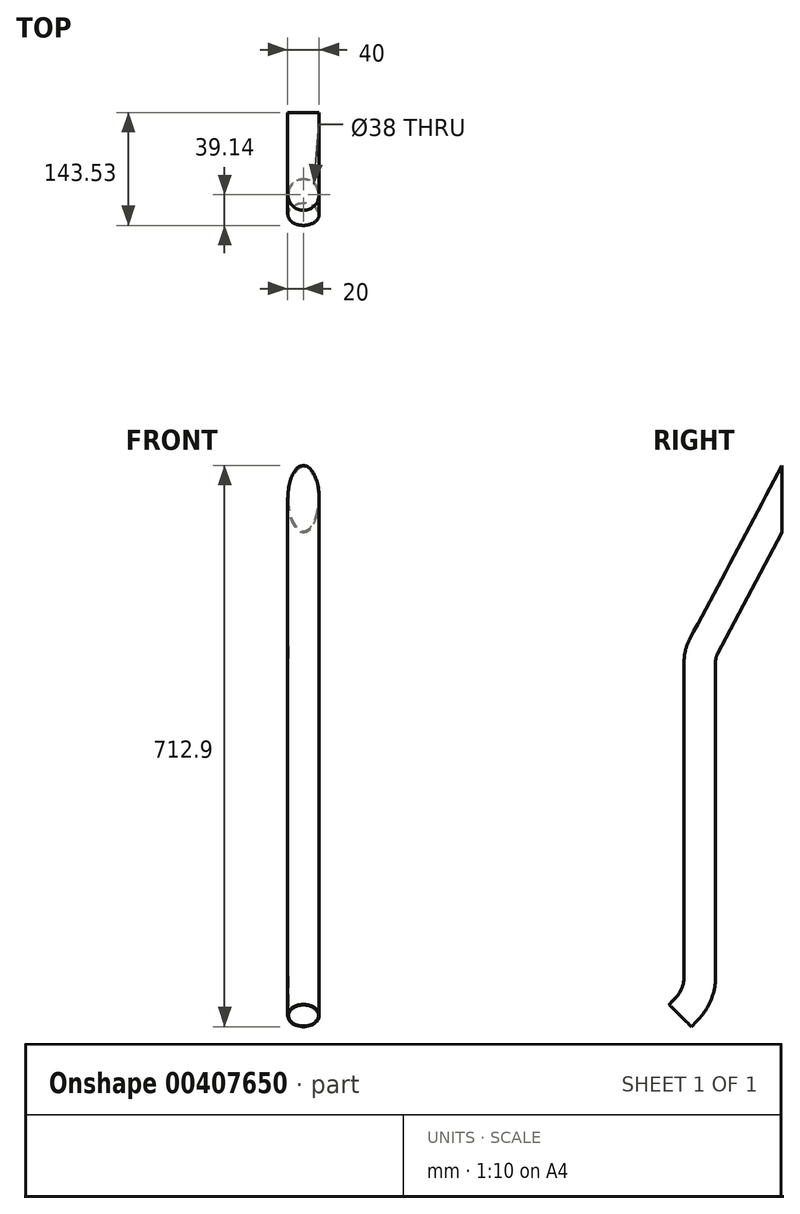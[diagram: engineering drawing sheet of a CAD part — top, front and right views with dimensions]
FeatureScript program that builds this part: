
annotation { "Feature Type Name" : "Feature", "Feature Type Description" : "" }
export const myFeature = defineFeature(function(context is Context, id is Id, definition is map)
    precondition{}
    {
        {
            var Q0;
            Q0=qCreatedBy(makeId("Right.planeOp"),FACE);
            var sketch = newSketch(context, id + "F0", { "sketchPlane" : qUnion([Q0])});
            skLineSegment(sketch, "E0", {"start": v(0, 0) * mm, "end": v(7.43, 7.43) * mm});
            skLineSegment(sketch, "E1", {"start": v(25, 49.85) * mm, "end": v(25, 449.85) * mm});
            skLineSegment(sketch, "E2", {"start": v(29.68, 468.63) * mm, "end": v(147.05, 689.37) * mm});
            skPoint(sketch, "E3.visualSharp", {"position": v(25, 25) * mm});
            skArc(sketch, "E3.filletArc", {"start": v(7.43, 7.43) * mm, "mid": v(20.43, 26.9) * mm, "end": v(25, 49.85) * mm});
            skPoint(sketch, "E4.visualSharp", {"position": v(25, 459.83) * mm});
            skArc(sketch, "E4.filletArc", {"start": v(29.68, 468.63) * mm, "mid": v(26.19, 459.53) * mm, "end": v(25, 449.85) * mm});
            skPoint(sketch, "E5.visualSharp", {"position": v(83.86, 570.52) * mm});
            skLineSegment(sketch, "E6", {"start": v(0, 0) * mm, "end": v(15.6, -15.6) * mm});
            skSolve(sketch);
        }
        {
            var Q0;
            Q0=sQuery(id+"F0.wireOp",EDGE,"E6");
            cPlane(context, id + "F1", {"entities" : qUnion([Q0]), "cplaneType" : CPlaneType.LINE_ANGLE, "offset" : 25 * mm, "angle" : 0 * degree, "width" : 150 * mm, "height" : 150 * mm});
        }
        {
            var Q0;
            Q0=qCreatedBy(id+"F1.planeOp",FACE);
            var sketch = newSketch(context, id + "F2", { "sketchPlane" : qUnion([Q0])});
            skCircle(sketch, "E7", {"center": v(0, 0) * mm, "radius": 20 * mm});
            skCircle(sketch, "E8.0", {"center": v(0, 0) * mm, "radius": 19 * mm});
            skSolve(sketch);
        }
        {
            var Q0;
            Q0=makeQuery(id+"F2.imprint","IMPRINT",FACE,{"disambiguationData":[TD([[makeQuery(id+"F2.imprint","IMPRINT",EDGE,{"derivedFrom":sQuery(id+"F2.wireOp",EDGE,"E7")}),1.0]])]});
            var Q1;
            Q1=sQuery(id+"F0.wireOp",EDGE,"E0");
            var Q2;
            Q2=sQuery(id+"F0.wireOp",EDGE,"E3.filletArc");
            var Q3;
            Q3=sQuery(id+"F0.wireOp",EDGE,"E1");
            var Q4;
            Q4=sQuery(id+"F0.wireOp",EDGE,"E2");
            var Q5;
            Q5=sQuery(id+"F0.wireOp",EDGE,"E4.filletArc");
            sweep(context, id + "F3", {"profiles" : qUnion([Q0]), "path" : qUnion([Q1, Q2, Q3, Q4, Q5])});
        }
        {
            var Q0;
            Q0=qCreatedBy(makeId("Right.planeOp"),FACE);
            var sketch = newSketch(context, id + "F4", { "sketchPlane" : qUnion([Q0])});
            skLineSegment(sketch, "E9.0", {"start": v(129.4, 698.76) * mm, "end": v(164.7, 679.98) * mm});
            skLineSegment(sketch, "E10", {"start": v(212.33, 769.54) * mm, "end": v(94.96, 548.8) * mm});
            skLineSegment(sketch, "E11", {"start": v(129.4, 698.76) * mm, "end": v(129.4, 613.56) * mm});
            skSolve(sketch);
        }
        {
            var Q0;
            {var subQ0=sQuery(id+"F4.wireOp",EDGE,"E9.0");Q0=makeQuery(id+"F4.imprint","IMPRINT",FACE,{"disambiguationData":[TD([[makeQuery(id+"F4.imprint","IMPRINT",EDGE,{"derivedFrom":subQ0}),-1.0]])]});}
            extrude(context, id + "F5", {"entities" : qUnion([Q0]), "operationType" : NewBodyOperationType.REMOVE, "oppositeDirection" : true, "depth" : 25 * mm});
        }
        {
            var Q0;
            {var subQ0=sQuery(id+"F4.wireOp",EDGE,"E9.0");Q0=makeQuery(id+"F4.imprint","IMPRINT",FACE,{"disambiguationData":[TD([[makeQuery(id+"F4.imprint","IMPRINT",EDGE,{"derivedFrom":subQ0}),-1.0]])]});}
            extrude(context, id + "F6", {"entities" : qUnion([Q0]), "operationType" : NewBodyOperationType.REMOVE, "depth" : 25 * mm});
        }
    });
